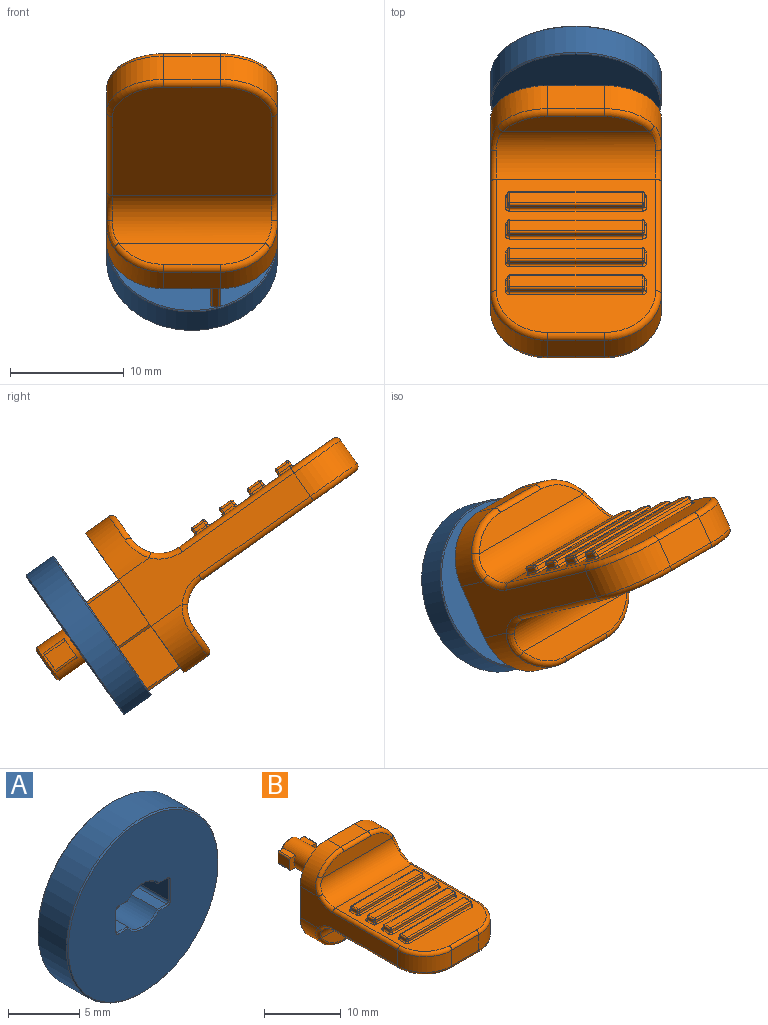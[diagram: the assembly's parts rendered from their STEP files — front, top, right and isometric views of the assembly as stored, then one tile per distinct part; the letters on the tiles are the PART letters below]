
ASSEMBLY  parts=2 mates=1
PART A: 41 faces, bbox 15x3x15 mm
  f0: plane 14.8x14.8mm, normal (0,1,0), area 155.9mm2, adj f28,f29,f30,f31,f32,f33,f34,f35
  f1: plane 14.8x14.8mm, normal (0,-1,0), area 155.9mm2, adj f15,f16,f17,f18,f19,f20,f21,f22
  f2: cylinder r=7.5mm len=15mm, axis (0,-1,0), area 131.9mm2, adj f27,f40
  f3: plane 2.8x0.91mm, normal (0,0,-1), area 2.6mm2, adj f10,f14,f22,f35
  f4: plane 2.8x1.8mm, normal (-1,0,0), area 5mm2, adj f11,f14,f26,f39
  f5: plane 2.8x0.91mm, normal (0,0,1), area 2.6mm2, adj f6,f11,f23,f36
  f6: cylinder r=1.85mm len=2.98mm, axis (0,1,0), area 9.7mm2, adj f5,f7,f21,f34
  f7: plane 2.8x0.91mm, normal (0,0,1), area 2.6mm2, adj f6,f12,f19,f32
  f8: plane 2.8x1.8mm, normal (1,0,0), area 5mm2, adj f12,f13,f15,f28
  f9: plane 2.8x0.91mm, normal (0,0,-1), area 2.6mm2, adj f10,f13,f18,f31
  f10: cylinder r=1.85mm len=2.98mm, axis (0,1,0), area 9.7mm2, adj f3,f9,f20,f33
  f11: cylinder r=0.2mm len=2.8mm, axis (0,-1,0), area 0.9mm2, adj f4,f5,f25,f38
  f12: cylinder r=0.2mm len=2.8mm, axis (0,1,0), area 0.9mm2, adj f7,f8,f17,f30
  f13: cylinder r=0.2mm len=2.8mm, axis (0,-1,0), area 0.9mm2, adj f8,f9,f16,f29
  f14: cylinder r=0.2mm len=2.8mm, axis (0,1,0), area 0.9mm2, adj f3,f4,f24,f37
  f15: plane 1.8x0.1mm, normal (0.71,-0.71,0), area 0.3mm2, adj f1,f8,f16,f17
  f16: cone r=0.3mm half-angle=45deg, axis (0,-1,0), area 0.1mm2, adj f1,f13,f15,f18
  f17: cone r=0.3mm half-angle=45deg, axis (0,-1,0), area 0.1mm2, adj f1,f12,f15,f19
  f18: plane 0.91x0.1mm, normal (0,-0.71,-0.71), area 0.1mm2, adj f1,f9,f16,f20
  f19: plane 0.91x0.1mm, normal (0,-0.71,0.71), area 0.1mm2, adj f1,f7,f17,f21
  f20: cone r=1.95mm half-angle=45deg, axis (0,-1,0), area 0.5mm2, adj f1,f10,f18,f22
  f21: cone r=1.95mm half-angle=45deg, axis (0,-1,0), area 0.5mm2, adj f1,f6,f19,f23
  f22: plane 0.91x0.1mm, normal (0,-0.71,-0.71), area 0.1mm2, adj f1,f3,f20,f24
  f23: plane 0.91x0.1mm, normal (0,-0.71,0.71), area 0.1mm2, adj f1,f5,f21,f25
  f24: cone r=0.3mm half-angle=45deg, axis (0,-1,0), area 0.1mm2, adj f1,f14,f22,f26
  f25: cone r=0.3mm half-angle=45deg, axis (0,-1,0), area 0.1mm2, adj f1,f11,f23,f26
  f26: plane 1.8x0.1mm, normal (-0.71,-0.71,0), area 0.3mm2, adj f1,f4,f24,f25
  f27: cone r=7.5mm half-angle=45deg, axis (0,1,0), area 6.6mm2, adj f1,f2
  f28: plane 1.8x0.1mm, normal (0.71,0.71,0), area 0.3mm2, adj f0,f8,f29,f30
  f29: cone r=0.3mm half-angle=45deg, axis (0,1,0), area 0.1mm2, adj f0,f13,f28,f31
  f30: cone r=0.3mm half-angle=45deg, axis (0,1,0), area 0.1mm2, adj f0,f12,f28,f32
  f31: plane 0.91x0.1mm, normal (0,0.71,-0.71), area 0.1mm2, adj f0,f9,f29,f33
  f32: plane 0.91x0.1mm, normal (0,0.71,0.71), area 0.1mm2, adj f0,f7,f30,f34
  f33: cone r=1.85mm half-angle=45deg, axis (0,1,0), area 0.5mm2, adj f0,f10,f31,f35
  f34: cone r=1.85mm half-angle=45deg, axis (0,1,0), area 0.5mm2, adj f0,f6,f32,f36
  f35: plane 0.91x0.1mm, normal (0,0.71,-0.71), area 0.1mm2, adj f0,f3,f33,f37
  f36: plane 0.91x0.1mm, normal (0,0.71,0.71), area 0.1mm2, adj f0,f5,f34,f38
  f37: cone r=0.3mm half-angle=45deg, axis (0,1,0), area 0.1mm2, adj f0,f14,f35,f39
  f38: cone r=0.3mm half-angle=45deg, axis (0,1,0), area 0.1mm2, adj f0,f11,f36,f39
  f39: plane 1.8x0.1mm, normal (-0.71,0.71,0), area 0.3mm2, adj f0,f4,f37,f38
  f40: cone r=7.4mm half-angle=45deg, axis (0,-1,0), area 6.6mm2, adj f0,f2
PART B: 171 faces, bbox 15.8x32.9x15.8 mm
  f0: plane 12.79x2.25mm, normal (0,-1,0), area 23.7mm2, adj f65,f85,f87,f89
  f1: plane 3.9x3.5mm, normal (0,0,-1), area 13.6mm2, adj f2,f7,f10,f59
  f2: plane 4.3x3.5mm, normal (-1,0,0), area 15mm2, adj f1,f7,f10,f60
  f3: plane 3.5x0.5mm, normal (0,0,-1), area 1.8mm2, adj f7,f10,f60,f61
  f4: plane 9.1x3.5mm, normal (1,0,0), area 31.9mm2, adj f7,f10,f61,f63
  f5: plane 4.6x3.5mm, normal (0,0,1), area 16.1mm2, adj f7,f10,f62,f63
  f6: plane 4.6x3.5mm, normal (-1,0,0), area 16.1mm2, adj f7,f10,f59,f62
  f7: plane 9.5x5mm, normal (0,1,0), area 19.3mm2, adj f1,f2,f3,f4,f5,f6,f8,f59
  f8: cylinder r=1.75mm len=5.8mm, axis (0,-1,0), area 54.4mm2, adj f7,f46,f47,f48,f49,f50,f51,f52
  f9: plane 3.1x3.1mm, normal (0,1,0), area 7.5mm2, adj f64
  f10: plane 15x15mm, normal (0,1,0), area 174.6mm2, adj f1,f2,f3,f4,f5,f6,f11,f12
  f11: plane 5x2.5mm, normal (0,0,1), area 12.5mm2, adj f10,f41,f44,f87
  f12: plane 18x5mm, normal (-1,0,0), area 55.3mm2, adj f10,f39,f41,f42,f77,f78,f86,f88
  f13: plane 5x2.5mm, normal (0,0,-1), area 12.5mm2, adj f10,f42,f43,f72
  f14: plane 18x5mm, normal (1,0,0), area 55.3mm2, adj f10,f40,f43,f44,f67,f69,f79,f81
  f15: plane 12.79x2.25mm, normal (0,-1,0), area 23.7mm2, adj f66,f70,f72,f74
  f16: plane 16.5x14mm, normal (0,0,1), area 128.6mm2, adj f65,f79,f80,f82,f84,f86,f93,f97
  f17: plane 16.5x14mm, normal (0,0,-1), area 222.3mm2, adj f66,f69,f71,f73,f75,f77
  f18: plane 5x2.5mm, normal (0,-1,0), area 12.5mm2, adj f39,f40,f73,f82
  f19: plane 11.6x0.35mm, normal (0,1,0), area 4.1mm2, adj f156,f165,f166,f170
  f20: plane 1.1x0.35mm, normal (-1,0,0), area 0.4mm2, adj f151,f155,f156,f157
  f21: plane 11.6x0.35mm, normal (0,-1,0), area 4.1mm2, adj f151,f154,f158,f159
  f22: plane 1.1x0.35mm, normal (1,0,0), area 0.4mm2, adj f159,f164,f167,f170
  f23: plane 11.6x1.1mm, normal (0,0,1), area 12.8mm2, adj f154,f155,f164,f165
  f24: plane 11.6x0.35mm, normal (0,1,0), area 4.1mm2, adj f139,f144,f147,f150
  f25: plane 1.1x0.35mm, normal (-1,0,0), area 0.4mm2, adj f136,f145,f146,f150
  f26: plane 11.6x0.35mm, normal (0,-1,0), area 4.1mm2, adj f131,f135,f136,f137
  f27: plane 1.1x0.35mm, normal (1,0,0), area 0.4mm2, adj f131,f134,f138,f139
  f28: plane 11.6x1.1mm, normal (0,0,1), area 12.8mm2, adj f134,f135,f144,f145
  f29: plane 11.6x0.35mm, normal (0,1,0), area 4.1mm2, adj f116,f125,f126,f130
  f30: plane 1.1x0.35mm, normal (-1,0,0), area 0.4mm2, adj f111,f115,f116,f117
  f31: plane 11.6x0.35mm, normal (0,-1,0), area 4.1mm2, adj f111,f114,f118,f119
  f32: plane 1.1x0.35mm, normal (1,0,0), area 0.4mm2, adj f119,f124,f127,f130
  f33: plane 11.6x1.1mm, normal (0,0,1), area 12.8mm2, adj f114,f115,f124,f125
  f34: plane 11.6x0.35mm, normal (0,1,0), area 4.1mm2, adj f96,f105,f106,f110
  f35: plane 1.1x0.35mm, normal (-1,0,0), area 0.4mm2, adj f91,f95,f96,f97
  f36: plane 11.6x0.35mm, normal (0,-1,0), area 4.1mm2, adj f91,f94,f98,f99
  f37: plane 1.1x0.35mm, normal (1,0,0), area 0.4mm2, adj f99,f104,f107,f110
  f38: plane 11.6x1.1mm, normal (0,0,1), area 12.8mm2, adj f94,f95,f104,f105
  f39: cylinder r=5mm len=5mm, axis (0,0,1), area 19.6mm2, adj f12,f18,f75,f84
  f40: cylinder r=5mm len=5mm, axis (0,0,-1), area 19.6mm2, adj f14,f18,f71,f80
  f41: cylinder r=5mm len=5mm, axis (0,-1,0), area 20.3mm2, adj f10,f11,f12,f89,f90
  f42: cylinder r=5mm len=5mm, axis (0,1,0), area 20.3mm2, adj f10,f12,f13,f74,f76
  f43: cylinder r=5mm len=5mm, axis (0,-1,0), area 20.3mm2, adj f10,f13,f14,f68,f70
  f44: cylinder r=5mm len=5mm, axis (0,1,0), area 20.3mm2, adj f10,f11,f14,f83,f85
  f45: plane 2.2x1.6mm, normal (-1,0,0), area 3.5mm2, adj f46,f47,f57,f58
  f46: plane 2x1.06mm, normal (0,-1,0), area 1.7mm2, adj f8,f45,f48,f49,f57,f58
  f47: plane 2x1.06mm, normal (0,1,0), area 1.7mm2, adj f8,f45,f48,f49,f57,f58
  f48: plane 2.2x0.86mm, normal (0,0,-1), area 1.9mm2, adj f8,f46,f47,f57
  f49: plane 2.2x0.86mm, normal (0,0,1), area 1.9mm2, adj f8,f46,f47,f58
  f50: plane 2.2x0.86mm, normal (0,0,1), area 1.9mm2, adj f8,f52,f53,f55
  f51: plane 2.2x0.86mm, normal (0,0,-1), area 1.9mm2, adj f8,f52,f53,f56
  f52: plane 2x1.06mm, normal (0,1,0), area 1.7mm2, adj f8,f50,f51,f54,f55,f56
  f53: plane 2x1.06mm, normal (0,-1,0), area 1.7mm2, adj f8,f50,f51,f54,f55,f56
  f54: plane 2.2x1.6mm, normal (1,0,0), area 3.5mm2, adj f52,f53,f55,f56
  f55: cylinder r=0.2mm len=2.2mm, axis (0,1,0), area 0.7mm2, adj f50,f52,f53,f54
  f56: cylinder r=0.2mm len=2.2mm, axis (0,-1,0), area 0.7mm2, adj f51,f52,f53,f54
  f57: cylinder r=0.2mm len=2.2mm, axis (0,1,0), area 0.7mm2, adj f45,f46,f47,f48
  f58: cylinder r=0.2mm len=2.2mm, axis (0,-1,0), area 0.7mm2, adj f45,f46,f47,f49
  f59: plane 3.5x0.2mm, normal (-0.71,0,-0.71), area 1mm2, adj f1,f6,f7,f10
  f60: plane 3.5x0.2mm, normal (-0.71,0,-0.71), area 1mm2, adj f2,f3,f7,f10
  f61: plane 3.5x0.2mm, normal (0.71,0,-0.71), area 1mm2, adj f3,f4,f7,f10
  f62: plane 3.5x0.2mm, normal (-0.71,0,0.71), area 1mm2, adj f5,f6,f7,f10
  f63: plane 3.5x0.2mm, normal (0.71,0,0.71), area 1mm2, adj f4,f5,f7,f10
  f64: cone r=1.55mm half-angle=45deg, axis (0,-1,0), area 2.9mm2, adj f8,f9
  f65: cylinder r=3mm len=14mm, axis (-1,0,0), area 65.2mm2, adj f0,f16,f81,f83,f88,f90
  f66: cylinder r=3mm len=14mm, axis (1,0,0), area 65.2mm2, adj f15,f17,f67,f68,f76,f78
  f67: torus R=3.5mm, axis (1,0,0), area 2.2mm2, adj f14,f66,f68,f69
  f68: bspline ~3.89x1.71mm, area 1.9mm2, adj f43,f66,f67,f70
  f69: cylinder r=0.5mm len=12mm, axis (0,-1,0), area 9.4mm2, adj f14,f17,f67,f71
  f70: torus R=4.5mm, axis (0,-1,0), area 4mm2, adj f15,f43,f68,f72
  f71: torus R=4.5mm, axis (0,0,1), area 5.9mm2, adj f17,f40,f69,f73
  f72: cylinder r=0.5mm len=5mm, axis (-1,0,0), area 3.9mm2, adj f13,f15,f70,f74
  f73: cylinder r=0.5mm len=5mm, axis (-1,0,0), area 3.9mm2, adj f17,f18,f71,f75
  f74: torus R=4.5mm, axis (0,-1,0), area 4mm2, adj f15,f42,f72,f76
  f75: torus R=4.5mm, axis (0,0,1), area 5.9mm2, adj f17,f39,f73,f77
  f76: bspline ~3.89x1.71mm, area 1.9mm2, adj f42,f66,f74,f78
  f77: cylinder r=0.5mm len=12mm, axis (0,1,0), area 9.4mm2, adj f12,f17,f75,f78
  f78: torus R=3.5mm, axis (1,0,0), area 2.2mm2, adj f12,f66,f76,f77
  f79: cylinder r=0.5mm len=12mm, axis (0,1,0), area 9.4mm2, adj f14,f16,f80,f81
  f80: torus R=4.5mm, axis (0,0,1), area 5.9mm2, adj f16,f40,f79,f82
  f81: torus R=3.5mm, axis (1,0,0), area 2.2mm2, adj f14,f65,f79,f83
  f82: cylinder r=0.5mm len=5mm, axis (1,0,0), area 3.9mm2, adj f16,f18,f80,f84
  f83: bspline ~3.89x1.71mm, area 1.9mm2, adj f44,f65,f81,f85
  f84: torus R=4.5mm, axis (0,0,1), area 5.9mm2, adj f16,f39,f82,f86
  f85: torus R=4.5mm, axis (0,-1,0), area 4mm2, adj f0,f44,f83,f87
  f86: cylinder r=0.5mm len=12mm, axis (0,-1,0), area 9.4mm2, adj f12,f16,f84,f88
  f87: cylinder r=0.5mm len=5mm, axis (1,0,0), area 3.9mm2, adj f0,f11,f85,f89
  f88: torus R=3.5mm, axis (1,0,0), area 2.2mm2, adj f12,f65,f86,f90
  f89: torus R=4.5mm, axis (0,-1,0), area 4mm2, adj f0,f41,f87,f90
  f90: bspline ~3.89x1.71mm, area 1.9mm2, adj f41,f65,f88,f89
  f91: cylinder r=0.2mm len=0.35mm, axis (0,0,-1), area 0.1mm2, adj f35,f36,f92,f93
  f92: sphere r=0.2mm, area 0.1mm2, adj f91,f94,f95
  f93: torus R=0.4mm, axis (0,0,1), area 0.1mm2, adj f16,f91,f97,f98
  f94: cylinder r=0.2mm len=11.6mm, axis (-1,0,0), area 3.6mm2, adj f36,f38,f92,f100
  f95: cylinder r=0.2mm len=1.1mm, axis (0,1,0), area 0.3mm2, adj f35,f38,f92,f101
  f96: cylinder r=0.2mm len=0.35mm, axis (0,0,1), area 0.1mm2, adj f34,f35,f101,f102
  f97: cylinder r=0.2mm len=1.1mm, axis (0,-1,0), area 0.3mm2, adj f16,f35,f93,f102
  f98: cylinder r=0.2mm len=11.6mm, axis (1,0,0), area 3.6mm2, adj f16,f36,f93,f103
  f99: cylinder r=0.2mm len=0.35mm, axis (0,0,1), area 0.1mm2, adj f36,f37,f100,f103
  f100: sphere r=0.2mm, area 0.1mm2, adj f94,f99,f104
  f101: sphere r=0.2mm, area 0.1mm2, adj f95,f96,f105
  f102: torus R=0.4mm, axis (0,0,1), area 0.1mm2, adj f16,f96,f97,f106
  f103: torus R=0.4mm, axis (0,0,1), area 0.1mm2, adj f16,f98,f99,f107
  f104: cylinder r=0.2mm len=1.1mm, axis (0,-1,0), area 0.3mm2, adj f37,f38,f100,f108
  f105: cylinder r=0.2mm len=11.6mm, axis (1,0,0), area 3.6mm2, adj f34,f38,f101,f108
  f106: cylinder r=0.2mm len=11.6mm, axis (-1,0,0), area 3.6mm2, adj f16,f34,f102,f109
  f107: cylinder r=0.2mm len=1.1mm, axis (0,1,0), area 0.3mm2, adj f16,f37,f103,f109
  f108: sphere r=0.2mm, area 0.1mm2, adj f104,f105,f110
  f109: torus R=0.4mm, axis (0,0,1), area 0.1mm2, adj f16,f106,f107,f110
  f110: cylinder r=0.2mm len=0.35mm, axis (0,0,-1), area 0.1mm2, adj f34,f37,f108,f109
  f111: cylinder r=0.2mm len=0.35mm, axis (0,0,-1), area 0.1mm2, adj f30,f31,f112,f113
  f112: sphere r=0.2mm, area 0.1mm2, adj f111,f114,f115
  f113: torus R=0.4mm, axis (0,0,1), area 0.1mm2, adj f16,f111,f117,f118
  f114: cylinder r=0.2mm len=11.6mm, axis (-1,0,0), area 3.6mm2, adj f31,f33,f112,f120
  f115: cylinder r=0.2mm len=1.1mm, axis (0,1,0), area 0.3mm2, adj f30,f33,f112,f121
  f116: cylinder r=0.2mm len=0.35mm, axis (0,0,1), area 0.1mm2, adj f29,f30,f121,f122
  f117: cylinder r=0.2mm len=1.1mm, axis (0,-1,0), area 0.3mm2, adj f16,f30,f113,f122
  f118: cylinder r=0.2mm len=11.6mm, axis (1,0,0), area 3.6mm2, adj f16,f31,f113,f123
  f119: cylinder r=0.2mm len=0.35mm, axis (0,0,1), area 0.1mm2, adj f31,f32,f120,f123
  f120: sphere r=0.2mm, area 0.1mm2, adj f114,f119,f124
  f121: sphere r=0.2mm, area 0.1mm2, adj f115,f116,f125
  f122: torus R=0.4mm, axis (0,0,1), area 0.1mm2, adj f16,f116,f117,f126
  f123: torus R=0.4mm, axis (0,0,1), area 0.1mm2, adj f16,f118,f119,f127
  f124: cylinder r=0.2mm len=1.1mm, axis (0,-1,0), area 0.3mm2, adj f32,f33,f120,f128
  f125: cylinder r=0.2mm len=11.6mm, axis (1,0,0), area 3.6mm2, adj f29,f33,f121,f128
  f126: cylinder r=0.2mm len=11.6mm, axis (-1,0,0), area 3.6mm2, adj f16,f29,f122,f129
  f127: cylinder r=0.2mm len=1.1mm, axis (0,1,0), area 0.3mm2, adj f16,f32,f123,f129
  f128: sphere r=0.2mm, area 0.1mm2, adj f124,f125,f130
  f129: torus R=0.4mm, axis (0,0,1), area 0.1mm2, adj f16,f126,f127,f130
  f130: cylinder r=0.2mm len=0.35mm, axis (0,0,-1), area 0.1mm2, adj f29,f32,f128,f129
  f131: cylinder r=0.2mm len=0.35mm, axis (0,0,1), area 0.1mm2, adj f26,f27,f132,f133
  f132: sphere r=0.2mm, area 0.1mm2, adj f131,f134,f135
  f133: torus R=0.4mm, axis (0,0,1), area 0.1mm2, adj f16,f131,f137,f138
  f134: cylinder r=0.2mm len=1.1mm, axis (0,-1,0), area 0.3mm2, adj f27,f28,f132,f140
  f135: cylinder r=0.2mm len=11.6mm, axis (-1,0,0), area 3.6mm2, adj f26,f28,f132,f141
  f136: cylinder r=0.2mm len=0.35mm, axis (0,0,-1), area 0.1mm2, adj f25,f26,f141,f142
  f137: cylinder r=0.2mm len=11.6mm, axis (1,0,0), area 3.6mm2, adj f16,f26,f133,f142
  f138: cylinder r=0.2mm len=1.1mm, axis (0,1,0), area 0.3mm2, adj f16,f27,f133,f143
  f139: cylinder r=0.2mm len=0.35mm, axis (0,0,-1), area 0.1mm2, adj f24,f27,f140,f143
  f140: sphere r=0.2mm, area 0.1mm2, adj f134,f139,f144
  f141: sphere r=0.2mm, area 0.1mm2, adj f135,f136,f145
  f142: torus R=0.4mm, axis (0,0,1), area 0.1mm2, adj f16,f136,f137,f146
  f143: torus R=0.4mm, axis (0,0,1), area 0.1mm2, adj f16,f138,f139,f147
  f144: cylinder r=0.2mm len=11.6mm, axis (1,0,0), area 3.6mm2, adj f24,f28,f140,f148
  f145: cylinder r=0.2mm len=1.1mm, axis (0,1,0), area 0.3mm2, adj f25,f28,f141,f148
  f146: cylinder r=0.2mm len=1.1mm, axis (0,-1,0), area 0.3mm2, adj f16,f25,f142,f149
  f147: cylinder r=0.2mm len=11.6mm, axis (-1,0,0), area 3.6mm2, adj f16,f24,f143,f149
  f148: sphere r=0.2mm, area 0.1mm2, adj f144,f145,f150
  f149: torus R=0.4mm, axis (0,0,1), area 0.1mm2, adj f16,f146,f147,f150
  f150: cylinder r=0.2mm len=0.35mm, axis (0,0,1), area 0.1mm2, adj f24,f25,f148,f149
  f151: cylinder r=0.2mm len=0.35mm, axis (0,0,-1), area 0.1mm2, adj f20,f21,f152,f153
  f152: sphere r=0.2mm, area 0.1mm2, adj f151,f154,f155
  f153: torus R=0.4mm, axis (0,0,1), area 0.1mm2, adj f16,f151,f157,f158
  f154: cylinder r=0.2mm len=11.6mm, axis (-1,0,0), area 3.6mm2, adj f21,f23,f152,f160
  f155: cylinder r=0.2mm len=1.1mm, axis (0,1,0), area 0.3mm2, adj f20,f23,f152,f161
  f156: cylinder r=0.2mm len=0.35mm, axis (0,0,1), area 0.1mm2, adj f19,f20,f161,f162
  f157: cylinder r=0.2mm len=1.1mm, axis (0,-1,0), area 0.3mm2, adj f16,f20,f153,f162
  f158: cylinder r=0.2mm len=11.6mm, axis (1,0,0), area 3.6mm2, adj f16,f21,f153,f163
  f159: cylinder r=0.2mm len=0.35mm, axis (0,0,1), area 0.1mm2, adj f21,f22,f160,f163
  f160: sphere r=0.2mm, area 0.1mm2, adj f154,f159,f164
  f161: sphere r=0.2mm, area 0.1mm2, adj f155,f156,f165
  f162: torus R=0.4mm, axis (0,0,1), area 0.1mm2, adj f16,f156,f157,f166
  f163: torus R=0.4mm, axis (0,0,1), area 0.1mm2, adj f16,f158,f159,f167
  f164: cylinder r=0.2mm len=1.1mm, axis (0,-1,0), area 0.3mm2, adj f22,f23,f160,f168
  f165: cylinder r=0.2mm len=11.6mm, axis (1,0,0), area 3.6mm2, adj f19,f23,f161,f168
  f166: cylinder r=0.2mm len=11.6mm, axis (-1,0,0), area 3.6mm2, adj f16,f19,f162,f169
  f167: cylinder r=0.2mm len=1.1mm, axis (0,1,0), area 0.3mm2, adj f16,f22,f163,f169
  f168: sphere r=0.2mm, area 0.1mm2, adj f164,f165,f170
  f169: torus R=0.4mm, axis (0,0,1), area 0.1mm2, adj f16,f166,f167,f170
  f170: cylinder r=0.2mm len=0.35mm, axis (0,0,-1), area 0.1mm2, adj f19,f22,f168,f169
PLACE A rot(axis=(-1,0,0),35.2deg) t=(6.95,-5.85,19.41)mm
PLACE B rot(axis=(-1,0,0),35.2deg) t=(6.95,11.75,6.99)mm
MATE slider B.f8 <-> A.f2  axis (0,-0.82,0.58) through (5.35,13.19,9.03)mm
